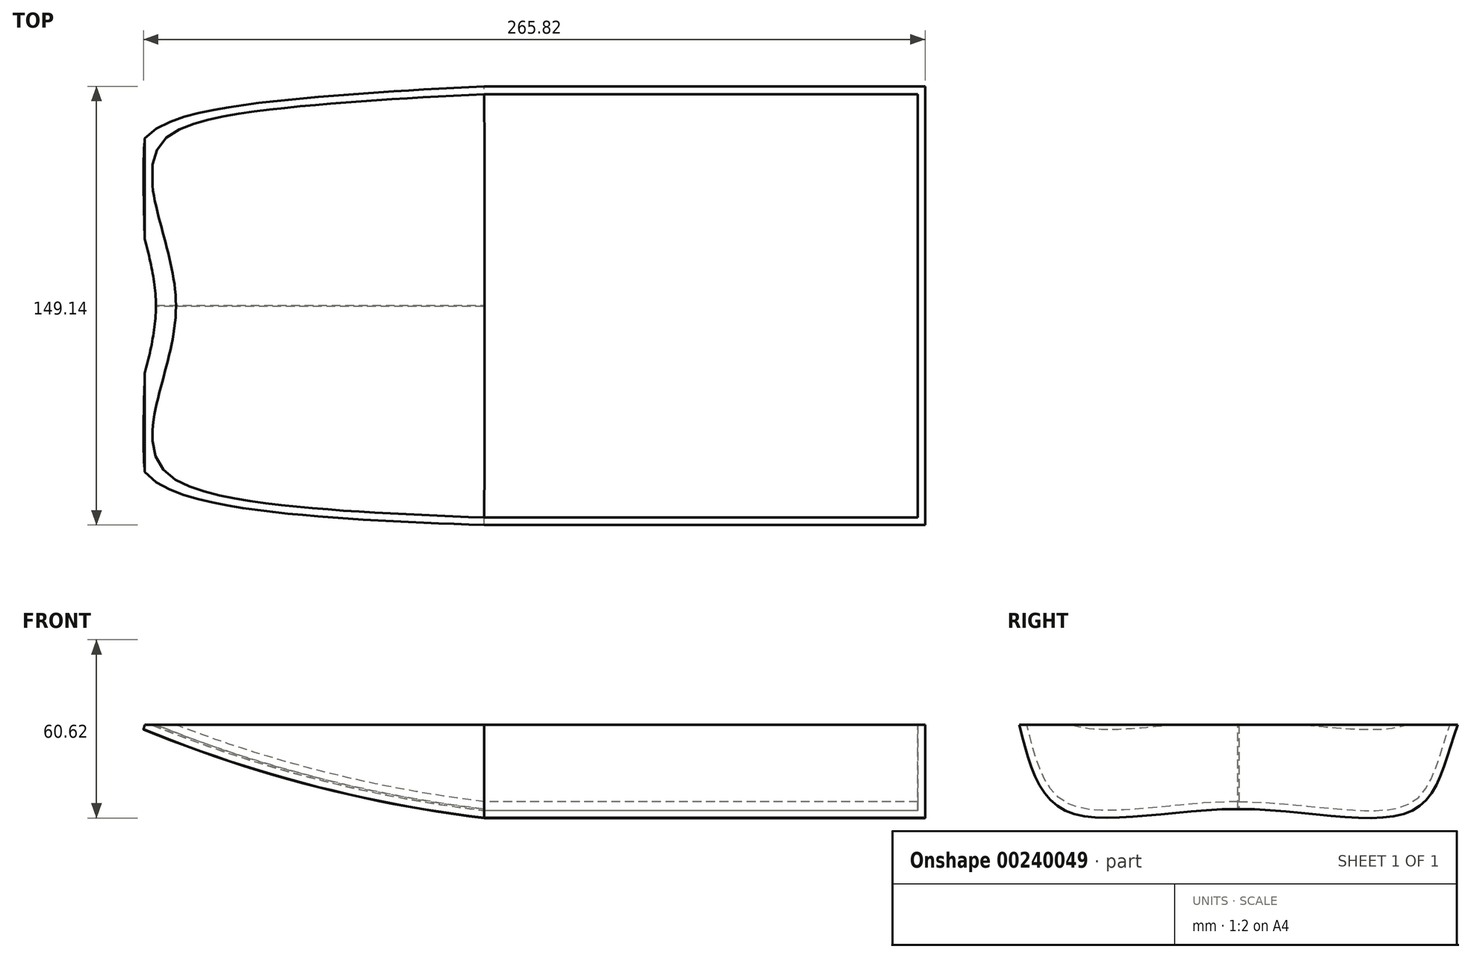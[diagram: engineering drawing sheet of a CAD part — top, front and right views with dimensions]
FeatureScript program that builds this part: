
annotation { "Feature Type Name" : "Feature", "Feature Type Description" : "" }
export const myFeature = defineFeature(function(context is Context, id is Id, definition is map)
    precondition{}
    {
        {
            var Q0;
            Q0=qCreatedBy(makeId("Front.planeOp"),FACE);
            var sketch = newSketch(context, id + "F0", { "sketchPlane" : qUnion([Q0])});
            skLineSegment(sketch, "E0.bottom", {"start": v(0, 0) * mm, "end": v(150, 0) * mm});
            skLineSegment(sketch, "E0.right", {"start": v(150, 0) * mm, "end": v(150, 30) * mm});
            skArc(sketch, "E1", {"start": v(-115, 30) * mm, "mid": v(-58.52, 11.1) * mm, "end": v(0, 0) * mm});
            skPoint(sketch, "E2.top.end.orphan", {"position": v(-115, 0) * mm});
            skSolve(sketch);
        }
        {
            var Q0;
            Q0=qCreatedBy(makeId("Right.planeOp"),FACE);
            cPlane(context, id + "F1", {"entities" : qUnion([Q0]), "cplaneType" : CPlaneType.OFFSET, "offset" : 150 * mm, "width" : 150 * mm, "height" : 150 * mm});
        }
        {
            var Q0;
            Q0=qCreatedBy(id+"F1.planeOp",FACE);
            var sketch = newSketch(context, id + "F2", { "sketchPlane" : qUnion([Q0])});
            skLineSegment(sketch, "E3.bottom", {"start": v(-75, 30) * mm, "end": v(75, 30) * mm});
            skLineSegment(sketch, "E3.top", {"start": v(-0.31, 0) * mm, "end": v(0, 0) * mm});
            skFitSpline(sketch, "E4", {"points": [v(-75, 30) * mm, v(-60, 0) * mm, v(0, 0) * mm, v(60, 0) * mm, v(75, 30) * mm], "startDerivative": vector(43.02, -173.66) * mm, "endDerivative": vector(65.03, 169.84) * mm});
            skPoint(sketch, "E5.orphan", {"position": v(-75, 0) * mm});
            skPoint(sketch, "E3.right.end.orphan", {"position": v(75, 0) * mm});
            skSolve(sketch);
        }
        {
            var Q0;
            {var subQ0=sQuery(id+"F2.wireOp",EDGE,"E3.bottom");Q0=makeQuery(id+"F2.imprint","IMPRINT",FACE,{"disambiguationData":[TD([[makeQuery(id+"F2.imprint","IMPRINT",EDGE,{"derivedFrom":subQ0}),-1.0]])]});}
            extrude(context, id + "F3", {"entities" : qUnion([Q0]), "oppositeDirection" : true, "depth" : 150 * mm});
        }
        {
            var Q0;
            Q0=makeQuery(id+"F3.opExtrude","CAP_FACE",FACE,{"disambiguationData":[OSD([sQuery(id+"F2.wireOp",EDGE,"E3.bottom"),sQuery(id+"F2.wireOp",EDGE,"E4")])],"isStart":false});
            var Q1;
            Q1=qSketchRegion(id+"F0",true);
            var Q2;
            Q2=sQuery(id+"F0.wireOp",EDGE,"E1");
            sweep(context, id + "F4", {"operationType" : NewBodyOperationType.ADD, "profiles" : qUnion([Q0, Q1]), "path" : qUnion([Q2])});
        }
        {
            var Q0;
            Q0=qCreatedBy(makeId("Front.planeOp"),FACE);
            var sketch = newSketch(context, id + "F5", { "sketchPlane" : qUnion([Q0])});
            skLineSegment(sketch, "E6.bottom", {"start": v(154.83, 28.62) * mm, "end": v(-132.64, 28.62) * mm});
            skLineSegment(sketch, "E6.top", {"start": v(154.83, 68.12) * mm, "end": v(-132.64, 68.12) * mm});
            skLineSegment(sketch, "E6.left", {"start": v(154.83, 28.62) * mm, "end": v(154.83, 68.12) * mm});
            skLineSegment(sketch, "E6.right", {"start": v(-132.64, 28.62) * mm, "end": v(-132.64, 68.12) * mm});
            skSolve(sketch);
        }
        {
            var Q0;
            Q0=qSketchRegion(id+"F5",true);
            extrude(context, id + "F6", {"entities" : qUnion([Q0]), "operationType" : NewBodyOperationType.REMOVE, "endBound" : BoundingType.SYMMETRIC, "oppositeDirection" : true, "depth" : 200 * mm});
        }
        {
            var Q0;
            Q0=makeQuery(id+"F6.boolean.opBoolean","COPY",FACE,{"derivedFrom":makeQuery(id+"F6.opExtrude","SWEPT_FACE",FACE,{"disambiguationData":[OSD([sQuery(id+"F5.wireOp",EDGE,"E6.bottom")])]})});
            shell(context, id + "F7", {"entities" : qUnion([Q0]), "thickness" : 2.5 * mm});
        }
    });
